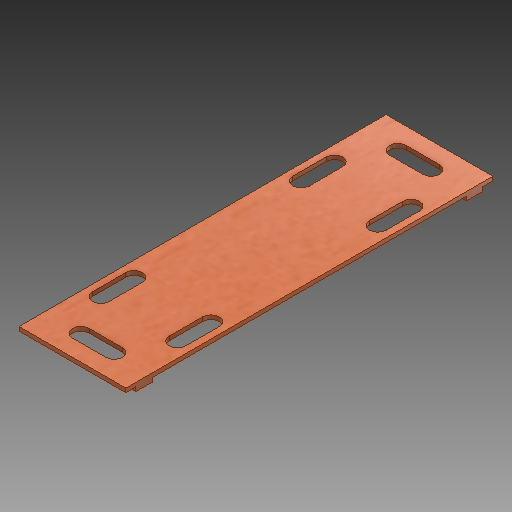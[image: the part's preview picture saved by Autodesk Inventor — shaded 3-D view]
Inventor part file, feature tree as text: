
AUTODESK INVENTOR PART (.ipt)
format: ipt  version: 2018 (Build 220112000, 112)  size: 219,136 bytes
history: native  units: mm
features: extrude x2, sketch x2, projected_geometry x1
ambient origin geometry x8: Origin, YZ Plane, XZ Plane, XY Plane, X Axis, Y Axis, Z Axis, Center Point
bodies: Body1 (feature_tree)
feature tree (5):
  extrude  "Extrusion2"  Depth=110.0mm
  extrude  "Extrusion3"  Depth=10.0mm
  sketch  "Skizze1"  dims[d0=32.0mm d1=110.0mm]
  sketch  "Skizze2"  dims[d4=10.0mm d5=10.0mm d6=10.0mm d7=5.0mm d8=5.0mm d9=5.0mm d10=5.0mm d11=5.0mm d12=2.0mm d13=2.0mm d14=50.0mm d15=5.0mm d16=1.2mm d17=0.0mm d18=5.0mm d19=5.0mm d20=5.0mm d21=5.0mm d22=3.0mm d23=0.0mm d24=0.0mm d25=3.0mm d26=1.2mm d27=0.0mm]
  projected_geometry  "Projizierte Kontur1"
